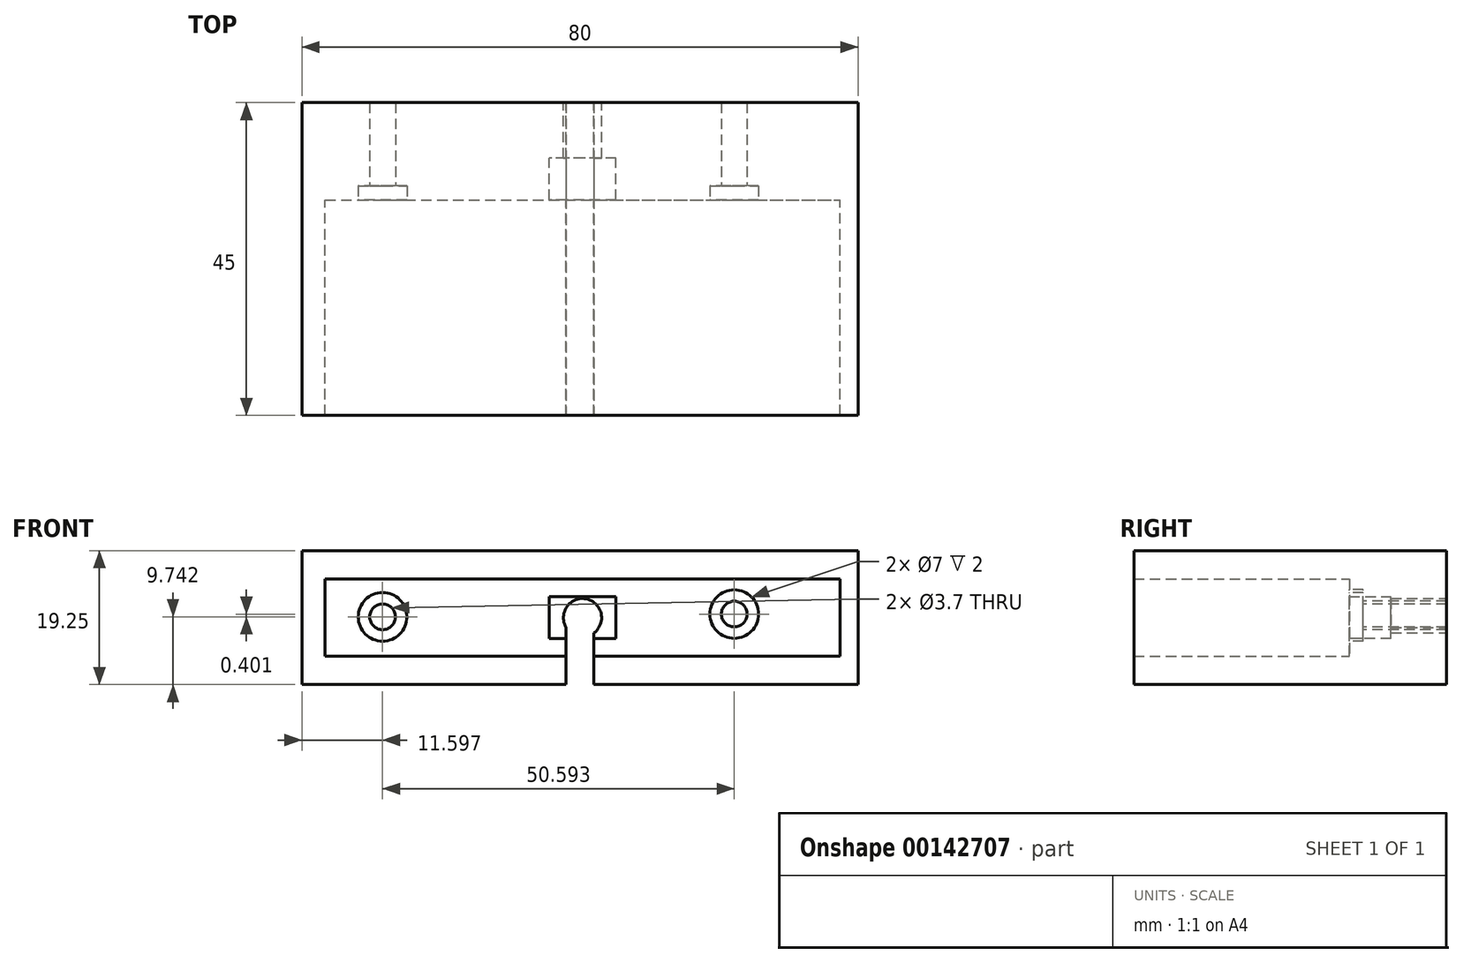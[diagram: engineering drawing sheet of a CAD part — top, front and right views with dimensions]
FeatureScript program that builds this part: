
annotation { "Feature Type Name" : "Feature", "Feature Type Description" : "" }
export const myFeature = defineFeature(function(context is Context, id is Id, definition is map)
    precondition{}
    {
        {
            var Q0;
            Q0=qCreatedBy(makeId("Front.planeOp"),FACE);
            var sketch = newSketch(context, id + "F0", { "sketchPlane" : qUnion([Q0])});
            skLineSegment(sketch, "E0.bottom", {"start": v(-58.85, 43.48) * mm, "end": v(15.2, 43.48) * mm});
            skLineSegment(sketch, "E0.top", {"start": v(-58.85, 32.38) * mm, "end": v(15.2, 32.38) * mm});
            skLineSegment(sketch, "E0.left", {"start": v(-58.85, 43.48) * mm, "end": v(-58.85, 32.38) * mm});
            skLineSegment(sketch, "E0.right", {"start": v(15.2, 43.48) * mm, "end": v(15.2, 32.38) * mm});
            skLineSegment(sketch, "E1.bottom", {"start": v(17.8, 28.3) * mm, "end": v(-62.2, 28.3) * mm});
            skLineSegment(sketch, "E1.top", {"start": v(17.8, 47.55) * mm, "end": v(-62.2, 47.55) * mm});
            skLineSegment(sketch, "E1.left", {"start": v(17.8, 28.3) * mm, "end": v(17.8, 47.55) * mm});
            skLineSegment(sketch, "E1.right", {"start": v(-62.2, 28.3) * mm, "end": v(-62.2, 47.55) * mm});
            skPoint(sketch, "E2", {"position": v(-58.85, 37.93) * mm});
            skPoint(sketch, "E3", {"position": v(-21.83, 43.48) * mm});
            skPoint(sketch, "E4", {"position": v(-21.83, 37.93) * mm});
            skLineSegment(sketch, "E5.bottom", {"start": v(-17.01, 34.93) * mm, "end": v(-26.64, 34.93) * mm});
            skLineSegment(sketch, "E5.top", {"start": v(-17.01, 40.93) * mm, "end": v(-26.64, 40.93) * mm});
            skLineSegment(sketch, "E5.left", {"start": v(-17.01, 34.93) * mm, "end": v(-17.01, 40.93) * mm});
            skLineSegment(sketch, "E5.right", {"start": v(-26.64, 34.93) * mm, "end": v(-26.64, 40.93) * mm});
            skCircle(sketch, "E6", {"center": v(-21.83, 37.93) * mm, "radius": 2.75 * mm});
            skSolve(sketch);
        }
        {
            var Q0;
            Q0=makeQuery(id+"F0.imprint","IMPRINT",FACE,{"disambiguationData":[TD([[makeQuery(id+"F0.imprint","IMPRINT",EDGE,{"derivedFrom":sQuery(id+"F0.wireOp",EDGE,"E0.bottom")}),1.0]])]});
            extrude(context, id + "F1", {"entities" : qUnion([Q0]), "offsetDistance" : 25 * mm, "depth" : 45 * mm});
        }
        {
            var Q0;
            Q0=makeQuery(id+"F0.imprint","IMPRINT",FACE,{"disambiguationData":[TD([[makeQuery(id+"F0.imprint","IMPRINT",EDGE,{"derivedFrom":sQuery(id+"F0.wireOp",EDGE,"E0.bottom")}),-1.0]])]});
            extrude(context, id + "F2", {"entities" : qUnion([Q0]), "operationType" : NewBodyOperationType.ADD, "offsetDistance" : 25 * mm, "depth" : 14 * mm});
        }
        {
            var Q0;
            Q0=makeQuery(id+"F0.imprint","IMPRINT",FACE,{"disambiguationData":[TD([[makeQuery(id+"F0.imprint","IMPRINT",EDGE,{"derivedFrom":sQuery(id+"F0.wireOp",EDGE,"E5.bottom")}),-1.0]])]});
            extrude(context, id + "F3", {"entities" : qUnion([Q0]), "operationType" : NewBodyOperationType.ADD, "depth" : 8 * mm});
        }
        {
            var Q0;
            Q0=makeQuery(id+"F1.opExtrude","SWEPT_FACE",FACE,{"disambiguationData":[OSD([sQuery(id+"F0.wireOp",EDGE,"E1.bottom")])]});
            cPlane(context, id + "F4", {"entities" : qUnion([Q0]), "cplaneType" : CPlaneType.OFFSET, "offset" : 0 * mm, "width" : 150 * mm, "height" : 150 * mm});
        }
        {
            var Q0;
            Q0=qCreatedBy(id+"F4.planeOp",FACE);
            var sketch = newSketch(context, id + "F5", { "sketchPlane" : qUnion([Q0])});
            skLineSegment(sketch, "E7.0.0", {"start": v(-62.2, 0) * mm, "end": v(17.8, 0) * mm});
            skLineSegment(sketch, "E7.0.1", {"start": v(17.8, 0) * mm, "end": v(17.8, 45) * mm});
            skLineSegment(sketch, "E7.0.2", {"start": v(17.8, 45) * mm, "end": v(-62.2, 45) * mm});
            skLineSegment(sketch, "E7.0.3", {"start": v(-62.2, 45) * mm, "end": v(-62.2, 0) * mm});
            skPoint(sketch, "E8", {"position": v(-62.2, 22.5) * mm});
            skPoint(sketch, "E9", {"position": v(-22.2, 45) * mm});
            skPoint(sketch, "E10", {"position": v(-22.2, 22.5) * mm});
            skLineSegment(sketch, "E11.bottom", {"start": v(-20.2, 15.94) * mm, "end": v(-24.2, 15.94) * mm});
            skLineSegment(sketch, "E11.top", {"start": v(-20.2, 74.06) * mm, "end": v(-24.2, 74.06) * mm});
            skLineSegment(sketch, "E11.left", {"start": v(-20.2, 15.94) * mm, "end": v(-20.2, 74.06) * mm});
            skLineSegment(sketch, "E11.right", {"start": v(-24.2, 15.94) * mm, "end": v(-24.2, 74.06) * mm});
            skLineSegment(sketch, "E12.bottom", {"start": v(-20.2, -0.81) * mm, "end": v(-24.2, -0.81) * mm});
            skLineSegment(sketch, "E12.top", {"start": v(-20.2, 90.81) * mm, "end": v(-24.2, 90.81) * mm});
            skLineSegment(sketch, "E12.left", {"start": v(-20.2, -0.81) * mm, "end": v(-20.2, 90.81) * mm});
            skLineSegment(sketch, "E12.right", {"start": v(-24.2, -0.81) * mm, "end": v(-24.2, 90.81) * mm});
            skSolve(sketch);
        }
        {
            var Q0;
            {var subQ5=sQuery(id+"F5.wireOp",EDGE,"E11.bottom");Q0=makeQuery(id+"F5.imprint","IMPRINT",FACE,{"disambiguationData":[TD([[makeQuery(id+"F5.imprint","IMPRINT",EDGE,{"derivedFrom":subQ5}),-1.0]])]});}
            extrude(context, id + "F6", {"entities" : qUnion([Q0]), "operationType" : NewBodyOperationType.REMOVE, "oppositeDirection" : true, "depth" : 3.07 * mm});
        }
        {
            var Q0;
            {var subQ0=sQuery(id+"F5.wireOp",EDGE,"E12.left");var subQ1=sQuery(id+"F5.wireOp",EDGE,"E7.0.2");var subQ2=makeQuery(id+"F5.imprint","INTERSECT",VERTEX,{"derivedFrom":[subQ1,subQ0]});Q0=makeQuery(id+"F5.imprint","IMPRINT",FACE,{"disambiguationData":[TD([[makeQuery(id+"F5.imprint","IMPRINT",EDGE,{"disambiguationData":[TD([[subQ2,-1.0]])],"derivedFrom":subQ1}),1.0]])]});}
            var Q1;
            {var subQ0=sQuery(id+"F5.wireOp",EDGE,"E11.bottom");Q1=makeQuery(id+"F5.imprint","IMPRINT",FACE,{"disambiguationData":[TD([[makeQuery(id+"F5.imprint","IMPRINT",EDGE,{"derivedFrom":subQ0}),1.0]])]});}
            extrude(context, id + "F7", {"entities" : qUnion([Q0, Q1]), "operationType" : NewBodyOperationType.REMOVE, "oppositeDirection" : true, "offsetDistance" : 25 * mm, "depth" : 8.28 * mm});
        }
        {
            var Q0;
            Q0=makeQuery(id+"F2.opExtrude","CAP_FACE",FACE,{"disambiguationData":[OSD([sQuery(id+"F0.wireOp",EDGE,"E0.bottom"),sQuery(id+"F0.wireOp",EDGE,"E0.top"),sQuery(id+"F0.wireOp",EDGE,"E0.left"),sQuery(id+"F0.wireOp",EDGE,"E0.right"),sQuery(id+"F0.wireOp",EDGE,"E5.bottom"),sQuery(id+"F0.wireOp",EDGE,"E5.top"),sQuery(id+"F0.wireOp",EDGE,"E5.left"),sQuery(id+"F0.wireOp",EDGE,"E5.right")])],"isStart":false});
            cPlane(context, id + "F8", {"entities" : qUnion([Q0]), "cplaneType" : CPlaneType.OFFSET, "offset" : 0 * mm, "width" : 150 * mm, "height" : 150 * mm});
        }
        {
            var Q0;
            Q0=qCreatedBy(id+"F8.planeOp",FACE);
            var sketch = newSketch(context, id + "F9", { "sketchPlane" : qUnion([Q0])});
            skPoint(sketch, "E13", {"position": v(-44.14, 37.92) * mm});
            skPoint(sketch, "E14", {"position": v(8.29, 37.92) * mm});
            skLineSegment(sketch, "E15.bottom", {"start": v(-44.36, 43.1) * mm, "end": v(-24.41, 43.1) * mm});
            skLineSegment(sketch, "E15.top", {"start": v(-44.36, 33.4) * mm, "end": v(-24.41, 33.4) * mm});
            skLineSegment(sketch, "E15.left", {"start": v(-44.36, 43.1) * mm, "end": v(-44.36, 33.4) * mm});
            skLineSegment(sketch, "E15.right", {"start": v(-24.41, 43.1) * mm, "end": v(-24.41, 33.4) * mm});
            skLineSegment(sketch, "E16.bottom", {"start": v(-10.07, 43.25) * mm, "end": v(11.6, 43.25) * mm});
            skLineSegment(sketch, "E16.top", {"start": v(-10.07, 33.55) * mm, "end": v(11.6, 33.55) * mm});
            skLineSegment(sketch, "E16.left", {"start": v(-10.07, 43.25) * mm, "end": v(-10.07, 33.55) * mm});
            skLineSegment(sketch, "E16.right", {"start": v(11.6, 43.25) * mm, "end": v(11.6, 33.55) * mm});
            skSolve(sketch);
        }
        {
            var Q0;
            Q0=qCreatedBy(id+"F4.planeOp",FACE);
            var sketch = newSketch(context, id + "F10", { "sketchPlane" : qUnion([Q0])});
            skLineSegment(sketch, "E17", {"start": v(-58.7, 7.08) * mm, "end": v(21.4, 7.08) * mm});
            skCircle(sketch, "E18", {"center": v(-47.3, 7.08) * mm, "radius": 1.87 * mm});
            skCircle(sketch, "E19", {"center": v(9, 7.08) * mm, "radius": 1.88 * mm});
            skCircle(sketch, "E20", {"center": v(-47.3, 7.08) * mm, "radius": 3.55 * mm});
            skCircle(sketch, "E21", {"center": v(9, 7.08) * mm, "radius": 3.55 * mm});
            skSolve(sketch);
        }
        {
            var Q0;
            Q0=qCreatedBy(id+"F8.planeOp",FACE);
            var sketch = newSketch(context, id + "F11", { "sketchPlane" : qUnion([Q0])});
            skCircle(sketch, "E22", {"center": v(-50.6, 38.04) * mm, "radius": 3.5 * mm});
            skCircle(sketch, "E23", {"center": v(-50.6, 38.04) * mm, "radius": 1.85 * mm});
            skCircle(sketch, "E24", {"center": v(0, 38.44) * mm, "radius": 3.5 * mm});
            skCircle(sketch, "E25", {"center": v(0, 38.44) * mm, "radius": 1.85 * mm});
            skSolve(sketch);
        }
        {
            var Q0;
            Q0=makeQuery(id+"F11.imprint","IMPRINT",FACE,{"disambiguationData":[TD([[makeQuery(id+"F11.imprint","IMPRINT",EDGE,{"derivedFrom":sQuery(id+"F11.wireOp",EDGE,"E22")}),1.0]])]});
            var Q1;
            Q1=makeQuery(id+"F11.imprint","IMPRINT",FACE,{"disambiguationData":[TD([[makeQuery(id+"F11.imprint","IMPRINT",EDGE,{"derivedFrom":sQuery(id+"F11.wireOp",EDGE,"E24")}),1.0]])]});
            extrude(context, id + "F12", {"entities" : qUnion([Q0, Q1]), "operationType" : NewBodyOperationType.REMOVE, "oppositeDirection" : true, "depth" : 2 * mm, "offsetDistance" : 25 * mm});
        }
        {
            var Q0;
            Q0=makeQuery(id+"F12.boolean.opBoolean","SPLIT",FACE,{"disambiguationData":[TD([makeQuery(id+"F12.opExtrude","SWEPT_FACE",FACE,{"disambiguationData":[OSD([sQuery(id+"F11.wireOp",EDGE,"E25")])]})])],"derivedFrom":makeQuery(id+"F2.opExtrude","CAP_FACE",FACE,{"disambiguationData":[OSD([sQuery(id+"F0.wireOp",EDGE,"E0.bottom"),sQuery(id+"F0.wireOp",EDGE,"E0.top"),sQuery(id+"F0.wireOp",EDGE,"E0.left"),sQuery(id+"F0.wireOp",EDGE,"E0.right"),sQuery(id+"F0.wireOp",EDGE,"E5.bottom"),sQuery(id+"F0.wireOp",EDGE,"E5.top"),sQuery(id+"F0.wireOp",EDGE,"E5.left"),sQuery(id+"F0.wireOp",EDGE,"E5.right")])],"isStart":false})});
            var Q1;
            Q1=makeQuery(id+"F12.boolean.opBoolean","SPLIT",FACE,{"disambiguationData":[TD([makeQuery(id+"F12.opExtrude","SWEPT_FACE",FACE,{"disambiguationData":[OSD([sQuery(id+"F11.wireOp",EDGE,"E23")])]})])],"derivedFrom":makeQuery(id+"F2.opExtrude","CAP_FACE",FACE,{"disambiguationData":[OSD([sQuery(id+"F0.wireOp",EDGE,"E0.bottom"),sQuery(id+"F0.wireOp",EDGE,"E0.top"),sQuery(id+"F0.wireOp",EDGE,"E0.left"),sQuery(id+"F0.wireOp",EDGE,"E0.right"),sQuery(id+"F0.wireOp",EDGE,"E5.bottom"),sQuery(id+"F0.wireOp",EDGE,"E5.top"),sQuery(id+"F0.wireOp",EDGE,"E5.left"),sQuery(id+"F0.wireOp",EDGE,"E5.right")])],"isStart":false})});
            extrude(context, id + "F13", {"entities" : qUnion([Q0, Q1]), "operationType" : NewBodyOperationType.REMOVE, "oppositeDirection" : true, "depth" : 25 * mm, "offsetDistance" : 25 * mm});
        }
    });
